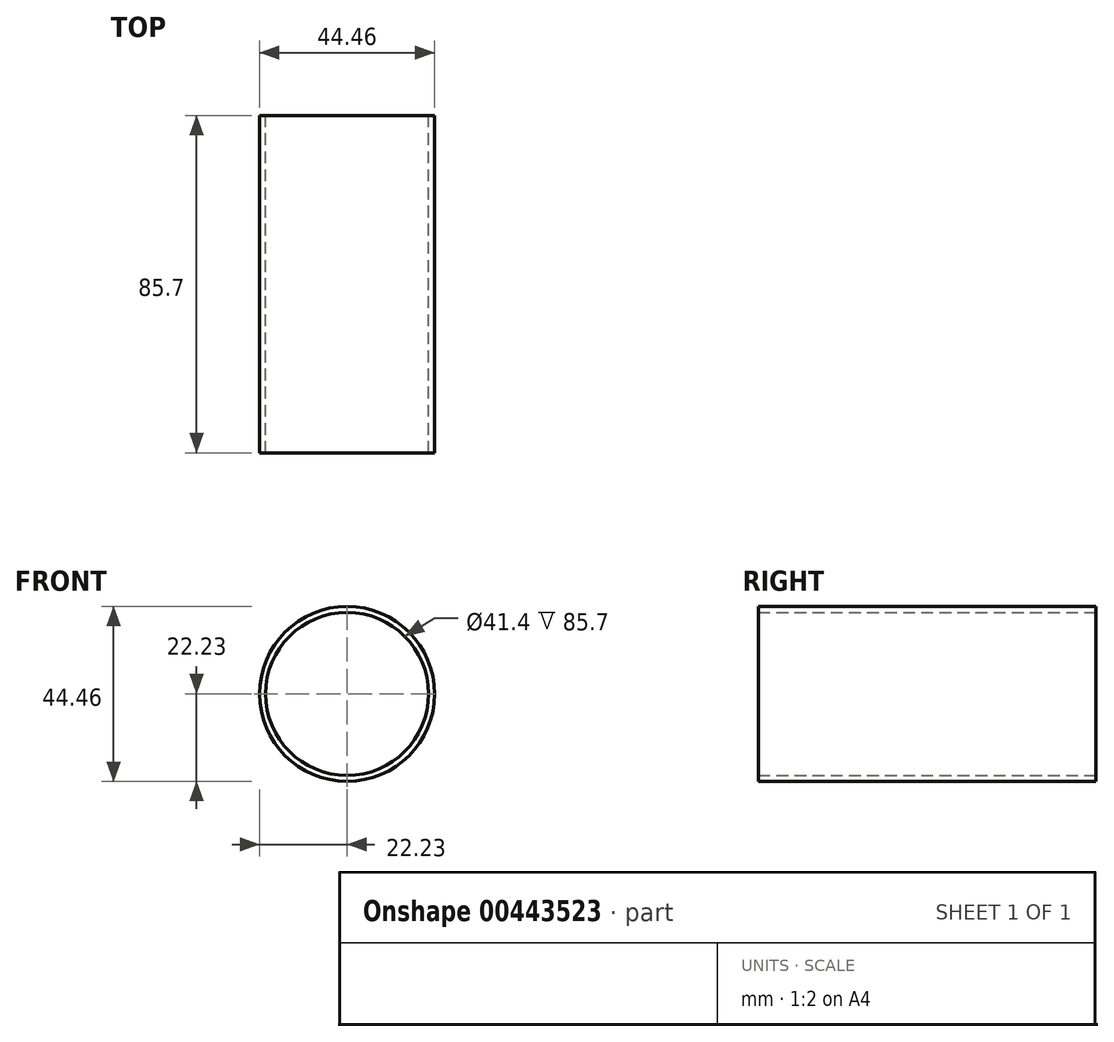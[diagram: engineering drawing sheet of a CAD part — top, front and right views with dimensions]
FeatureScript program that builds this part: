
annotation { "Feature Type Name" : "Feature", "Feature Type Description" : "" }
export const myFeature = defineFeature(function(context is Context, id is Id, definition is map)
    precondition{}
    {
        {
            var Q0;
            Q0=qCreatedBy(makeId("Front.planeOp"),FACE);
            var sketch = newSketch(context, id + "F0", { "sketchPlane" : qUnion([Q0])});
            skCircle(sketch, "E0", {"center": v(0, 0) * mm, "radius": 20.7 * mm});
            skCircle(sketch, "E1", {"center": v(0, 0) * mm, "radius": 22.23 * mm});
            skSolve(sketch);
        }
        {
            var Q0;
            Q0=makeQuery(id+"F0.imprint","IMPRINT",FACE,{"disambiguationData":[TD([[makeQuery(id+"F0.imprint","IMPRINT",EDGE,{"derivedFrom":sQuery(id+"F0.wireOp",EDGE,"E0")}),-1.0]])]});
            extrude(context, id + "F1", {"entities" : qUnion([Q0]), "depth" : 85.7 * mm});
        }
    });
